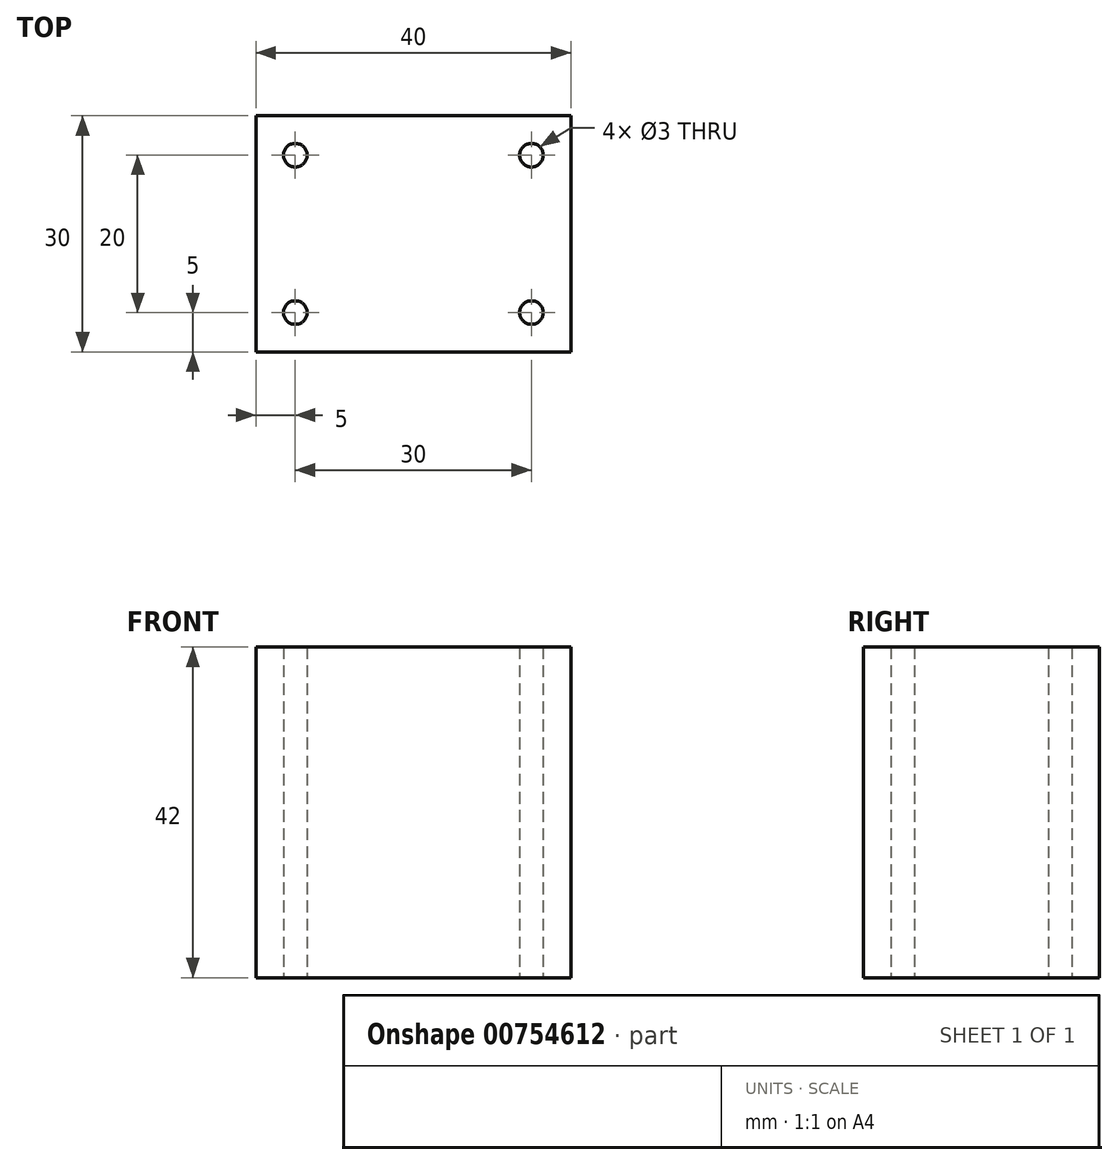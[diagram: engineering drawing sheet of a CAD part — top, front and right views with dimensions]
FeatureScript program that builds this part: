
annotation { "Feature Type Name" : "Feature", "Feature Type Description" : "" }
export const myFeature = defineFeature(function(context is Context, id is Id, definition is map)
    precondition{}
    {
        {
            var Q0;
            Q0=qCreatedBy(makeId("Top.planeOp"),FACE);
            var sketch = newSketch(context, id + "F0", { "sketchPlane" : qUnion([Q0])});
            skLineSegment(sketch, "E0.bottom", {"start": v(0, 0) * mm, "end": v(40, 0) * mm});
            skLineSegment(sketch, "E0.top", {"start": v(0, 30) * mm, "end": v(40, 30) * mm});
            skLineSegment(sketch, "E0.left", {"start": v(0, 0) * mm, "end": v(0, 30) * mm});
            skLineSegment(sketch, "E0.right", {"start": v(40, 0) * mm, "end": v(40, 30) * mm});
            skLineSegment(sketch, "E1.0", {"start": v(5, 25) * mm, "end": v(35, 25) * mm, "construction": true});
            skLineSegment(sketch, "E1.1", {"start": v(5, 5) * mm, "end": v(5, 25) * mm, "construction": true});
            skLineSegment(sketch, "E1.2", {"start": v(5, 5) * mm, "end": v(35, 5) * mm, "construction": true});
            skLineSegment(sketch, "E1.3", {"start": v(35, 5) * mm, "end": v(35, 25) * mm, "construction": true});
            skCircle(sketch, "E2", {"center": v(5, 25) * mm, "radius": 1.5 * mm});
            skCircle(sketch, "E3", {"center": v(35, 25) * mm, "radius": 1.5 * mm});
            skCircle(sketch, "E4", {"center": v(35, 5) * mm, "radius": 1.5 * mm});
            skCircle(sketch, "E5", {"center": v(5, 5) * mm, "radius": 1.5 * mm});
            skSolve(sketch);
        }
        {
            var Q0;
            Q0=makeQuery(id+"F0.imprint","IMPRINT",FACE,{"disambiguationData":[TD([[makeQuery(id+"F0.imprint","IMPRINT",EDGE,{"derivedFrom":sQuery(id+"F0.wireOp",EDGE,"E0.bottom")}),1.0]])]});
            extrude(context, id + "F1", {"entities" : qUnion([Q0]), "depth" : 42 * mm, "offsetDistance" : 25.4 * mm});
        }
    });
